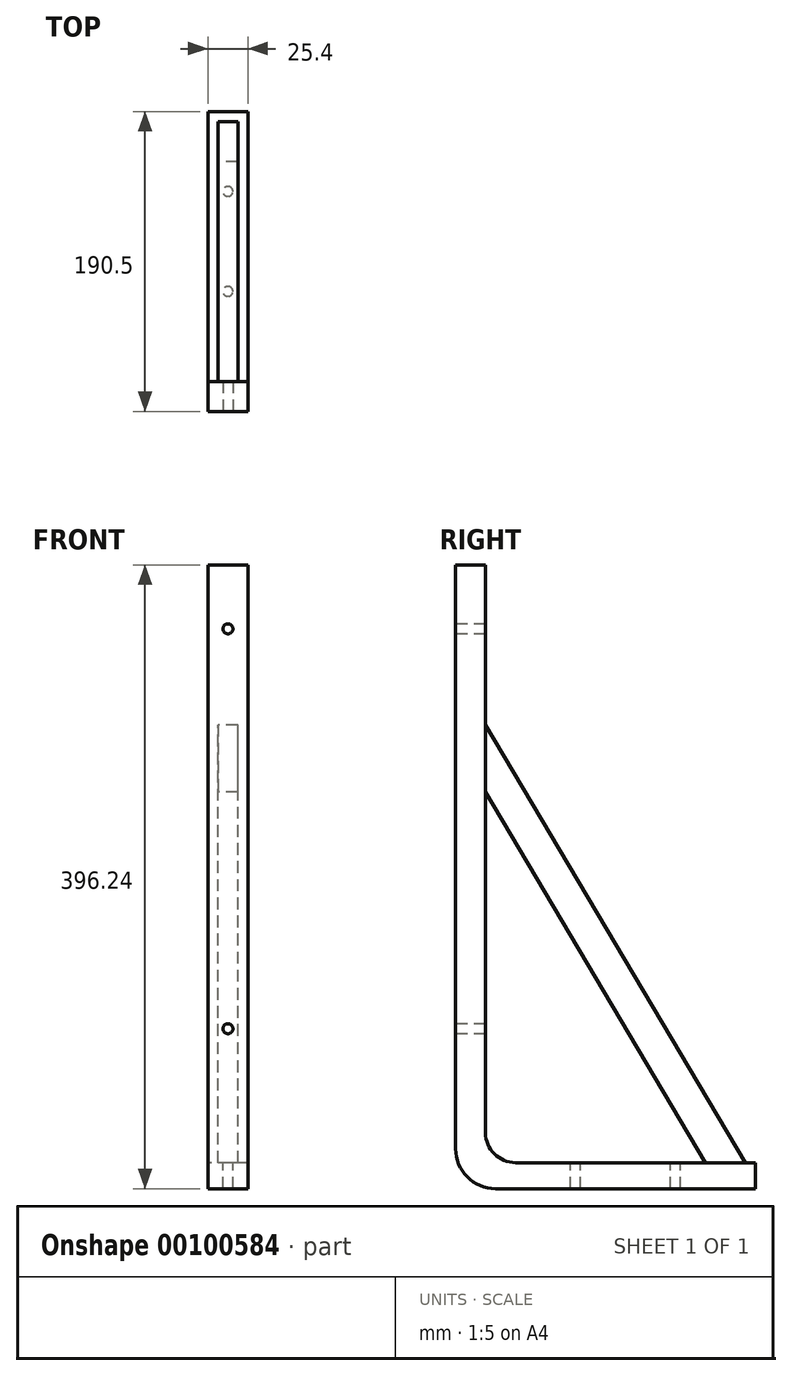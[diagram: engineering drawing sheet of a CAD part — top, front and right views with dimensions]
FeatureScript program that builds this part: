
annotation { "Feature Type Name" : "Feature", "Feature Type Description" : "" }
export const myFeature = defineFeature(function(context is Context, id is Id, definition is map)
    precondition{}
    {
        {
            var Q0;
            Q0=qCreatedBy(makeId("Right.planeOp"),FACE);
            var sketch = newSketch(context, id + "F0", { "sketchPlane" : qUnion([Q0])});
            skLineSegment(sketch, "E0", {"start": v(0, 0) * mm, "end": v(0, -396.24) * mm});
            skLineSegment(sketch, "E1", {"start": v(0, -396.24) * mm, "end": v(190.5, -396.24) * mm});
            skLineSegment(sketch, "E2", {"start": v(0, 0) * mm, "end": v(19.05, 0) * mm});
            skLineSegment(sketch, "E3", {"start": v(19.05, 0) * mm, "end": v(19.05, -379.73) * mm});
            skLineSegment(sketch, "E4", {"start": v(19.05, -379.73) * mm, "end": v(190.5, -379.73) * mm});
            skLineSegment(sketch, "E5", {"start": v(190.5, -379.73) * mm, "end": v(190.5, -396.24) * mm});
            skSolve(sketch);
        }
        {
            var Q0;
            Q0=makeQuery(id+"F0.imprint","IMPRINT",FACE,{"disambiguationData":[TD([[makeQuery(id+"F0.imprint","IMPRINT",EDGE,{"derivedFrom":sQuery(id+"F0.wireOp",EDGE,"E0")}),1.0]])]});
            extrude(context, id + "F1", {"entities" : qUnion([Q0]), "depth" : 25.4 * mm});
        }
        {
            var Q0;
            Q0=makeQuery(id+"F1.opExtrude","SWEPT_EDGE",EDGE,{"disambiguationData":[OSD([sQuery(id+"F0.wireOp",EDGE,"E0"),sQuery(id+"F0.wireOp",EDGE,"E1")])]});
            fillet(context, id + "F2", {"entities" : qUnion([Q0]), "radius" : 25.4 * mm, "tangentPropagation" : true, "allowEdgeOverflow" : false});
        }
        {
            var Q0;
            Q0=makeQuery(id+"F1.opExtrude","SWEPT_EDGE",EDGE,{"disambiguationData":[OSD([sQuery(id+"F0.wireOp",EDGE,"E3"),sQuery(id+"F0.wireOp",EDGE,"E4")])]});
            fillet(context, id + "F3", {"entities" : qUnion([Q0]), "radius" : 19.05 * mm, "tangentPropagation" : true, "allowEdgeOverflow" : false});
        }
        {
            var Q0;
            Q0=makeQuery(id+"F1.opExtrude","CAP_FACE",FACE,{"disambiguationData":[OSD([sQuery(id+"F0.wireOp",EDGE,"E0"),sQuery(id+"F0.wireOp",EDGE,"E1"),sQuery(id+"F0.wireOp",EDGE,"E2"),sQuery(id+"F0.wireOp",EDGE,"E3"),sQuery(id+"F0.wireOp",EDGE,"E4"),sQuery(id+"F0.wireOp",EDGE,"E5")])],"isStart":true});
            var sketch = newSketch(context, id + "F4", { "sketchPlane" : qUnion([Q0])});
            skLineSegment(sketch, "E6", {"start": v(-184.15, -379.73) * mm, "end": v(-19.05, -101.6) * mm});
            skLineSegment(sketch, "E7", {"start": v(-158.75, -379.73) * mm, "end": v(-19.05, -144.39) * mm});
            skLineSegment(sketch, "E8", {"start": v(-19.05, -144.39) * mm, "end": v(-19.05, -101.6) * mm});
            skLineSegment(sketch, "E9", {"start": v(-184.15, -379.73) * mm, "end": v(-158.75, -379.73) * mm});
            skSolve(sketch);
        }
        {
            var Q0;
            Q0=makeQuery(id+"F4.imprint","IMPRINT",FACE,{"disambiguationData":[TD([[makeQuery(id+"F4.imprint","IMPRINT",EDGE,{"derivedFrom":sQuery(id+"F4.wireOp",EDGE,"E6")}),-1.0]])]});
            extrude(context, id + "F5", {"entities" : qUnion([Q0]), "operationType" : NewBodyOperationType.ADD, "oppositeDirection" : true, "depth" : 25.4 * mm});
        }
        {
            var Q0;
            Q0=makeQuery(id+"F5.boolean.opBoolean","MERGE",FACE,{"derivedFrom":[makeQuery(id+"F1.opExtrude","CAP_FACE",FACE,{"disambiguationData":[OSD([sQuery(id+"F0.wireOp",EDGE,"E0"),sQuery(id+"F0.wireOp",EDGE,"E1"),sQuery(id+"F0.wireOp",EDGE,"E2"),sQuery(id+"F0.wireOp",EDGE,"E3"),sQuery(id+"F0.wireOp",EDGE,"E4"),sQuery(id+"F0.wireOp",EDGE,"E5")])],"isStart":true}),makeQuery(id+"F5.opExtrude","CAP_FACE",FACE,{"disambiguationData":[OSD([sQuery(id+"F4.wireOp",EDGE,"E6"),sQuery(id+"F4.wireOp",EDGE,"E7"),sQuery(id+"F4.wireOp",EDGE,"E8"),sQuery(id+"F4.wireOp",EDGE,"E9")])],"isStart":true})]});
            var sketch = newSketch(context, id + "F6", { "sketchPlane" : qUnion([Q0])});
            skLineSegment(sketch, "E10", {"start": v(-19.05, -101.6) * mm, "end": v(-19.05, -144.39) * mm});
            skLineSegment(sketch, "E11", {"start": v(-19.05, -144.39) * mm, "end": v(-158.75, -379.73) * mm});
            skLineSegment(sketch, "E12", {"start": v(-158.75, -379.73) * mm, "end": v(-184.15, -379.73) * mm});
            skLineSegment(sketch, "E13", {"start": v(-184.15, -379.73) * mm, "end": v(-19.05, -101.6) * mm});
            skSolve(sketch);
        }
        {
            var Q0;
            Q0=makeQuery(id+"F6.imprint","IMPRINT",FACE,{"disambiguationData":[TD([[makeQuery(id+"F6.imprint","IMPRINT",EDGE,{"derivedFrom":sQuery(id+"F6.wireOp",EDGE,"E10")}),-1.0]])]});
            extrude(context, id + "F7", {"entities" : qUnion([Q0]), "operationType" : NewBodyOperationType.REMOVE, "oppositeDirection" : true, "depth" : 6.35 * mm});
        }
        {
            var Q0;
            Q0=makeQuery(id+"F5.boolean.opBoolean","MERGE",FACE,{"derivedFrom":[makeQuery(id+"F1.opExtrude","CAP_FACE",FACE,{"disambiguationData":[OSD([sQuery(id+"F0.wireOp",EDGE,"E0"),sQuery(id+"F0.wireOp",EDGE,"E1"),sQuery(id+"F0.wireOp",EDGE,"E2"),sQuery(id+"F0.wireOp",EDGE,"E3"),sQuery(id+"F0.wireOp",EDGE,"E4"),sQuery(id+"F0.wireOp",EDGE,"E5")])],"isStart":false}),makeQuery(id+"F5.opExtrude","CAP_FACE",FACE,{"disambiguationData":[OSD([sQuery(id+"F4.wireOp",EDGE,"E6"),sQuery(id+"F4.wireOp",EDGE,"E7"),sQuery(id+"F4.wireOp",EDGE,"E8"),sQuery(id+"F4.wireOp",EDGE,"E9")])],"isStart":false})]});
            var sketch = newSketch(context, id + "F8", { "sketchPlane" : qUnion([Q0])});
            skLineSegment(sketch, "E14", {"start": v(184.15, -379.73) * mm, "end": v(158.75, -379.73) * mm});
            skLineSegment(sketch, "E15", {"start": v(158.75, -379.73) * mm, "end": v(19.05, -144.39) * mm});
            skLineSegment(sketch, "E16", {"start": v(19.05, -144.39) * mm, "end": v(19.05, -101.6) * mm});
            skLineSegment(sketch, "E17", {"start": v(19.05, -101.6) * mm, "end": v(184.15, -379.73) * mm});
            skSolve(sketch);
        }
        {
            var Q0;
            Q0=makeQuery(id+"F8.imprint","IMPRINT",FACE,{"disambiguationData":[TD([[makeQuery(id+"F8.imprint","IMPRINT",EDGE,{"derivedFrom":sQuery(id+"F8.wireOp",EDGE,"E14")}),-1.0]])]});
            extrude(context, id + "F9", {"entities" : qUnion([Q0]), "operationType" : NewBodyOperationType.REMOVE, "oppositeDirection" : true, "depth" : 6.35 * mm});
        }
        {
            var Q0;
            {var subQ2=sQuery(id+"F4.wireOp",EDGE,"E7");var subQ5=sQuery(id+"F0.wireOp",EDGE,"E4");var subQ7=sQuery(id+"F0.wireOp",EDGE,"E5");var subQ14=makeQuery(id+"F1.opExtrude","SWEPT_FACE",FACE,{"disambiguationData":[OSD([subQ5])]});Q0=makeQuery(id+"F9.boolean.opBoolean","MERGE",FACE,{"derivedFrom":[makeQuery(id+"F7.boolean.opBoolean","MERGE",FACE,{"derivedFrom":[makeQuery(id+"F5.boolean.opBoolean","SPLIT",FACE,{"disambiguationData":[TD([makeQuery(id+"F1.opExtrude","SWEPT_FACE",FACE,{"disambiguationData":[OSD([subQ7])]})])],"derivedFrom":subQ14}),makeQuery(id+"F5.boolean.opBoolean","SPLIT",FACE,{"disambiguationData":[TD([makeQuery(id+"F5.opExtrude","SWEPT_FACE",FACE,{"disambiguationData":[OSD([subQ2])]})])],"derivedFrom":subQ14}),makeQuery(id+"F7.opExtrude","SWEPT_FACE",FACE,{"disambiguationData":[OSD([sQuery(id+"F6.wireOp",EDGE,"E12")])]})]}),makeQuery(id+"F9.opExtrude","SWEPT_FACE",FACE,{"disambiguationData":[OSD([sQuery(id+"F8.wireOp",EDGE,"E14")])]})]});}
            var sketch = newSketch(context, id + "F10", { "sketchPlane" : qUnion([Q0])});
            skCircle(sketch, "E18", {"center": v(12.7, 76.2) * mm, "radius": 3.18 * mm});
            skPoint(sketch, "E18.centerSnap0", {"position": v(12.7, 38.1) * mm});
            skCircle(sketch, "E19", {"center": v(12.7, 139.7) * mm, "radius": 3.18 * mm});
            skLineSegment(sketch, "E20.0", {"start": v(0, 0) * mm, "end": v(25.4, 0) * mm});
            skSolve(sketch);
        }
        {
            var Q0;
            Q0 = qSketchRegion(id + "F10", true);
            extrude(context, id + "F11", {"entities" : qUnion([Q0]), "operationType" : NewBodyOperationType.REMOVE, "oppositeDirection" : true, "depth" : 25.4 * mm});
        }
        {
            var Q0;
            Q0=makeQuery(id+"F1.opExtrude","SWEPT_FACE",FACE,{"disambiguationData":[OSD([sQuery(id+"F0.wireOp",EDGE,"E0")])]});
            var sketch = newSketch(context, id + "F12", { "sketchPlane" : qUnion([Q0])});
            skCircle(sketch, "E21", {"center": v(12.7, -40.64) * mm, "radius": 3.18 * mm});
            skPoint(sketch, "E21.centerSnap0", {"position": v(12.7, 0) * mm});
            skCircle(sketch, "E22", {"center": v(12.7, -294.64) * mm, "radius": 3.18 * mm});
            skPoint(sketch, "E22.centerSnap0", {"position": v(12.7, -370.84) * mm});
            skLineSegment(sketch, "E23.0", {"start": v(25.4, -396.24) * mm, "end": v(0, -396.24) * mm});
            skSolve(sketch);
        }
        {
            var Q0;
            Q0=makeQuery(id+"F12.imprint","IMPRINT",FACE,{"disambiguationData":[TD([[makeQuery(id+"F12.imprint","IMPRINT",EDGE,{"derivedFrom":sQuery(id+"F12.wireOp",EDGE,"E21")}),1.0]])]});
            var Q1;
            Q1=makeQuery(id+"F12.imprint","IMPRINT",FACE,{"disambiguationData":[TD([[makeQuery(id+"F12.imprint","IMPRINT",EDGE,{"derivedFrom":sQuery(id+"F12.wireOp",EDGE,"E22")}),1.0]])]});
            extrude(context, id + "F13", {"entities" : qUnion([Q0, Q1]), "operationType" : NewBodyOperationType.REMOVE, "oppositeDirection" : true, "depth" : 25.4 * mm});
        }
    });
